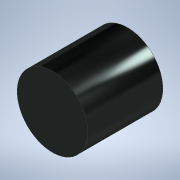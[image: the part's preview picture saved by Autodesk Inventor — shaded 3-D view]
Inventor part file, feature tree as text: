
AUTODESK INVENTOR PART (.ipt)
format: ipt  version: 2020 (Build 240168000, 168)  size: 109,056 bytes
history: native  units: mm
features: extrude x1, sketch x1
ambient origin geometry x8: Origin, YZ Plane, XZ Plane, XY Plane, X Axis, Y Axis, Z Axis, Center Point
bodies: Solid1 (feature_tree)
feature tree (2):
  extrude  "Extrusion1"  Depth=80.0mm TaperAngle=0.0deg
  sketch  "Sketch1"  dims[d0=75.0mm d1=80.0mm d2=0.0mm]
